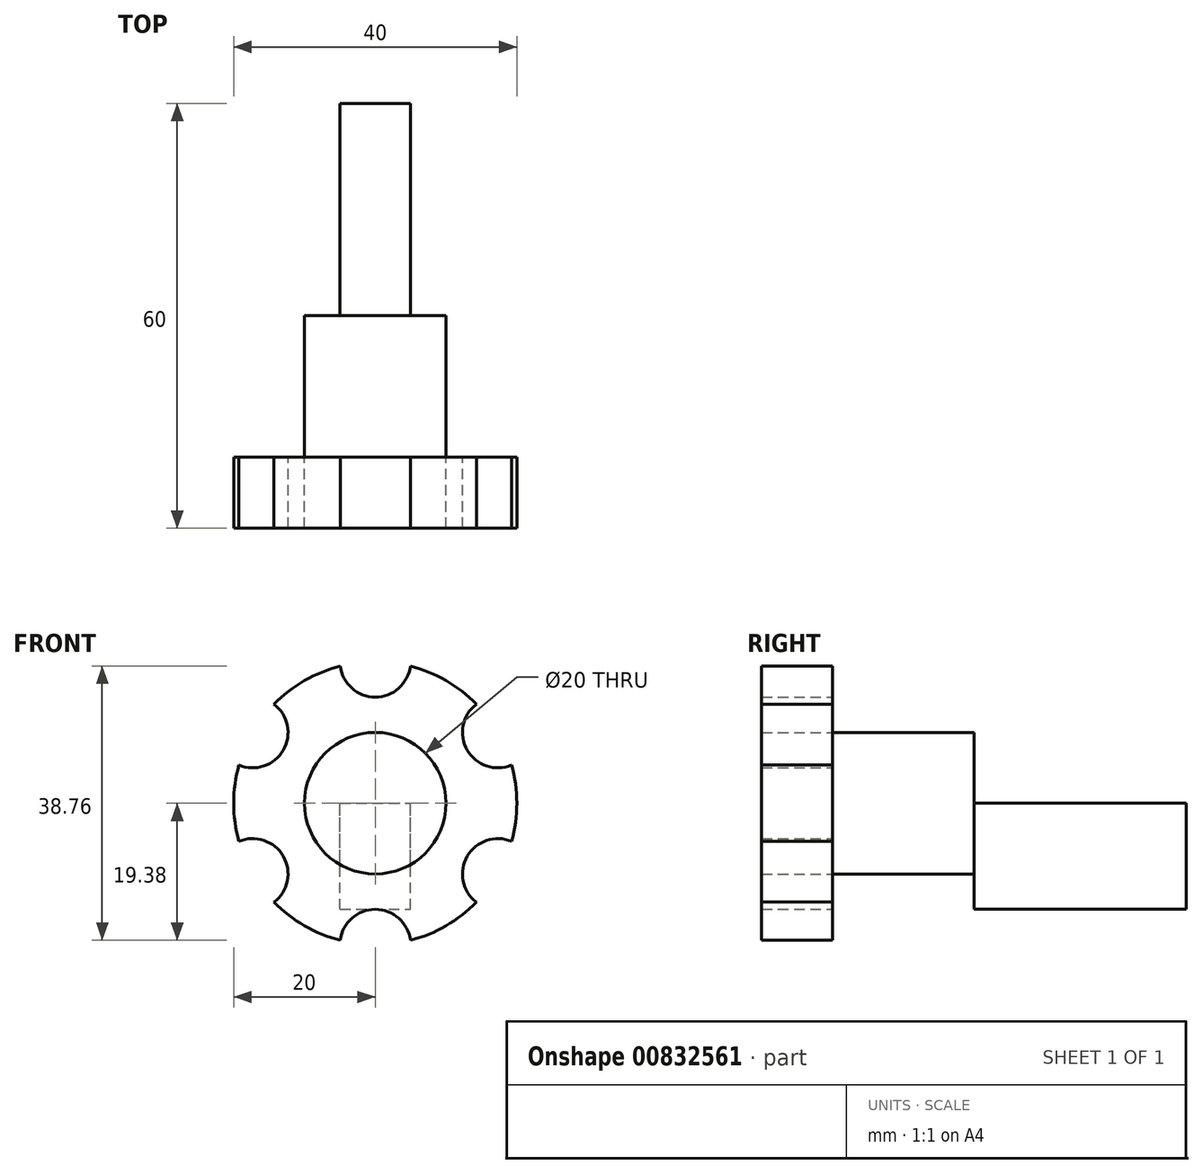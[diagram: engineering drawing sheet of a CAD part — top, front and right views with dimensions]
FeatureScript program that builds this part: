
annotation { "Feature Type Name" : "Feature", "Feature Type Description" : "" }
export const myFeature = defineFeature(function(context is Context, id is Id, definition is map)
    precondition{}
    {
        {
            var Q0;
            Q0=qCreatedBy(makeId("Front.planeOp"),FACE);
            var sketch = newSketch(context, id + "F0", { "sketchPlane" : qUnion([Q0])});
            skCircle(sketch, "E0", {"center": v(0, 0) * mm, "radius": 10 * mm});
            skSolve(sketch);
        }
        {
            var Q0;
            Q0 = qSketchRegion(id + "F0", true);
            extrude(context, id + "F1", {"entities" : qUnion([Q0]), "depth" : 20 * mm, "offsetDistance" : 25 * mm});
        }
        {
            var Q0;
            Q0=makeQuery(id+"F1.opExtrude","CAP_FACE",FACE,{"disambiguationData":[OSD([sQuery(id+"F0.wireOp",EDGE,"E0")])],"isStart":false});
            var sketch = newSketch(context, id + "F2", { "sketchPlane" : qUnion([Q0])});
            skCircle(sketch, "E1", {"center": v(0, 0) * mm, "radius": 20 * mm});
            skCircle(sketch, "E2", {"center": v(0, 20) * mm, "radius": 5 * mm});
            skCircle(sketch, "E3.1.0", {"center": v(-17.32, 10) * mm, "radius": 5 * mm});
            skCircle(sketch, "E3.2.0", {"center": v(-17.32, -10) * mm, "radius": 5 * mm});
            skCircle(sketch, "E3.3.0", {"center": v(0, -20) * mm, "radius": 5 * mm});
            skCircle(sketch, "E3.4.0", {"center": v(17.32, -10) * mm, "radius": 5 * mm});
            skCircle(sketch, "E3.5.0", {"center": v(17.32, 10) * mm, "radius": 5 * mm});
            skSolve(sketch);
        }
        {
            var Q0;
            Q0=makeQuery(id+"F2.imprint","IMPRINT",FACE,{"disambiguationData":[TD([[makeQuery(id+"F2.imprint","IMPRINT",EDGE,{"derivedFrom":makeQuery(id+"F1.opExtrude","CAP_EDGE",EDGE,{"disambiguationData":[OSD([sQuery(id+"F0.wireOp",EDGE,"E0")])],"isStart":false})}),-1.0]])]});
            extrude(context, id + "F3", {"entities" : qUnion([Q0]), "depth" : 10 * mm, "offsetDistance" : 25 * mm});
        }
        {
            var Q0;
            Q0=makeQuery(id+"F1.opExtrude","CAP_FACE",FACE,{"disambiguationData":[OSD([sQuery(id+"F0.wireOp",EDGE,"E0")])],"isStart":false});
            var sketch = newSketch(context, id + "F4", { "sketchPlane" : qUnion([Q0])});
            skSolve(sketch);
        }
        {
            var Q0;
            Q0=makeQuery(id+"F4.imprint","IMPRINT",FACE,{"disambiguationData":[TD([[makeQuery(id+"F4.imprint","IMPRINT",EDGE,{"derivedFrom":makeQuery(id+"F1.opExtrude","CAP_EDGE",EDGE,{"disambiguationData":[OSD([sQuery(id+"F0.wireOp",EDGE,"E0")])],"isStart":false})}),1.0]])]});
            extrude(context, id + "F5", {"entities" : qUnion([Q0]), "depth" : 10 * mm, "offsetDistance" : 25 * mm});
        }
        {
            var Q0;
            Q0=qCreatedBy(makeId("Top.planeOp"),FACE);
            var sketch = newSketch(context, id + "F6", { "sketchPlane" : qUnion([Q0])});
            skLineSegment(sketch, "E4.bottom", {"start": v(-5, 0) * mm, "end": v(5, 0) * mm});
            skLineSegment(sketch, "E4.top", {"start": v(-5, 30) * mm, "end": v(5, 30) * mm});
            skLineSegment(sketch, "E4.left", {"start": v(-5, 0) * mm, "end": v(-5, 30) * mm});
            skLineSegment(sketch, "E4.right", {"start": v(5, 0) * mm, "end": v(5, 30) * mm});
            skSolve(sketch);
        }
        {
            var Q0;
            Q0=makeQuery(id+"F6.imprint","IMPRINT",FACE,{"disambiguationData":[TD([[makeQuery(id+"F6.imprint","IMPRINT",EDGE,{"derivedFrom":sQuery(id+"F6.wireOp",EDGE,"E4.bottom")}),1.0]])]});
            extrude(context, id + "F7", {"entities" : qUnion([Q0]), "operationType" : NewBodyOperationType.ADD, "oppositeDirection" : true, "depth" : 15 * mm, "offsetDistance" : 25 * mm});
        }
    });
